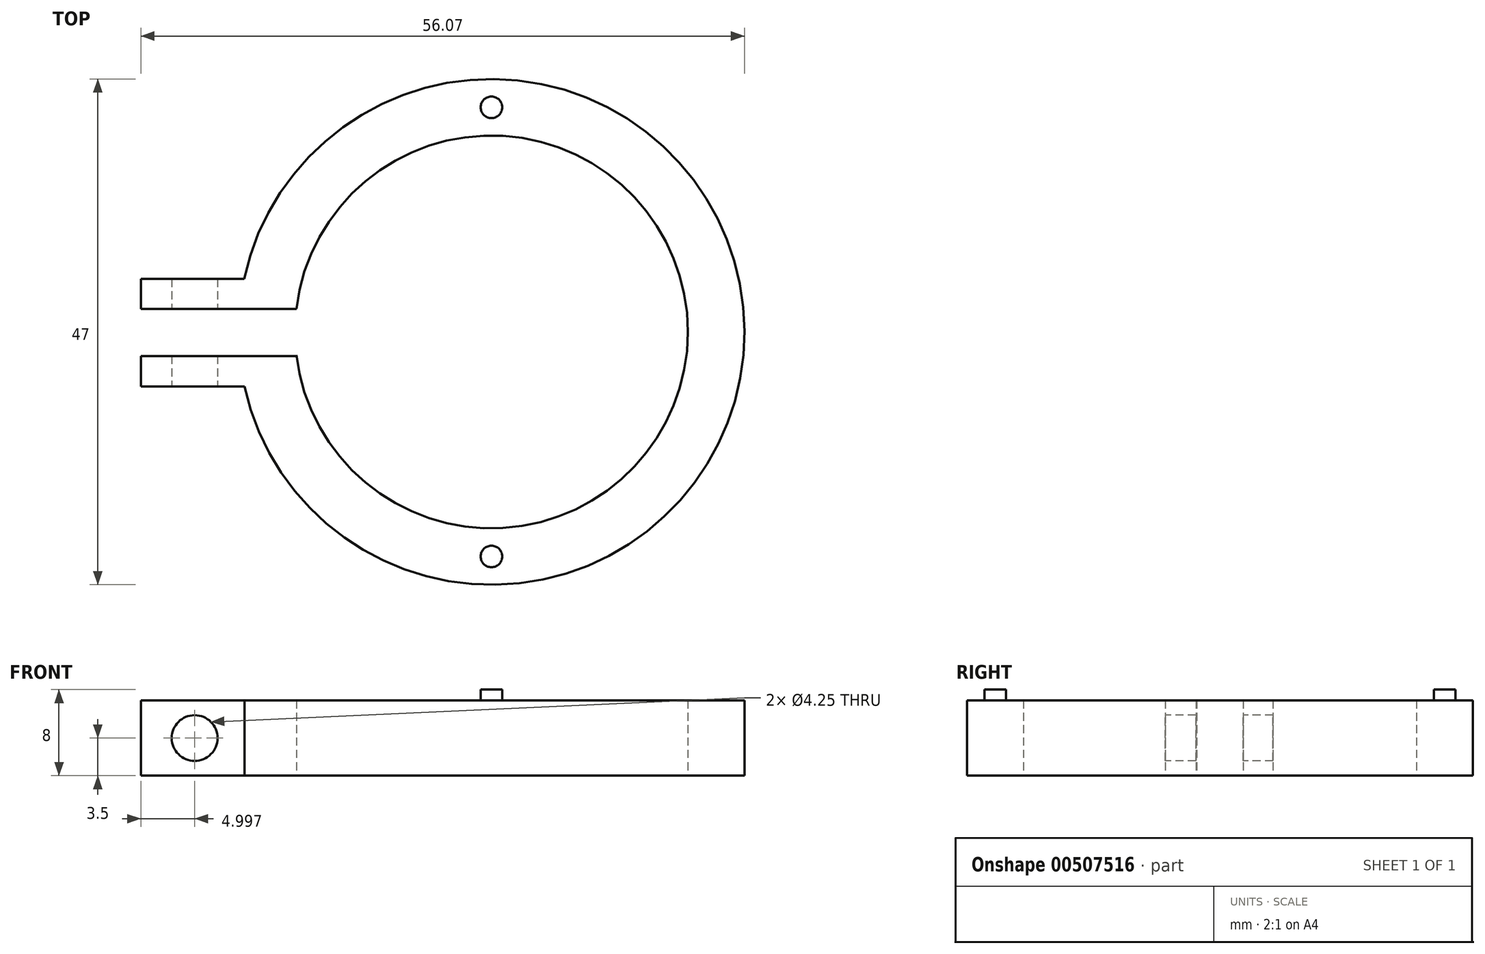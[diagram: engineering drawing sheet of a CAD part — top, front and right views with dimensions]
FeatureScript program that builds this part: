
annotation { "Feature Type Name" : "Feature", "Feature Type Description" : "" }
export const myFeature = defineFeature(function(context is Context, id is Id, definition is map)
    precondition{}
    {
        {
            var Q0;
            Q0=qCreatedBy(makeId("Top.planeOp"),FACE);
            var sketch = newSketch(context, id + "F0", { "sketchPlane" : qUnion([Q0])});
            skCircle(sketch, "E0", {"center": v(0, 0) * mm, "radius": 23.5 * mm});
            skCircle(sketch, "E1", {"center": v(0, 0) * mm, "radius": 18.25 * mm});
            skLineSegment(sketch, "E2.bottom", {"start": v(-17.57, 4.92) * mm, "end": v(-32.57, 4.92) * mm});
            skLineSegment(sketch, "E2.top", {"start": v(-17.57, -5.08) * mm, "end": v(-32.57, -5.08) * mm});
            skLineSegment(sketch, "E2.left", {"start": v(-17.57, 4.92) * mm, "end": v(-17.57, -5.08) * mm});
            skLineSegment(sketch, "E2.right", {"start": v(-32.57, 4.92) * mm, "end": v(-32.57, -5.08) * mm});
            skLineSegment(sketch, "E3.bottom", {"start": v(-18.12, 2.15) * mm, "end": v(-32.57, 2.15) * mm});
            skLineSegment(sketch, "E3.top", {"start": v(-18.12, -2.24) * mm, "end": v(-32.57, -2.24) * mm});
            skLineSegment(sketch, "E3.left", {"start": v(-18.12, 2.15) * mm, "end": v(-18.12, -2.24) * mm});
            skLineSegment(sketch, "E3.right", {"start": v(-32.57, 2.15) * mm, "end": v(-32.57, -2.24) * mm});
            skSolve(sketch);
        }
        {
            var Q0;
            {var subQ0=sQuery(id+"F0.wireOp",EDGE,"E2.bottom");var subQ1=sQuery(id+"F0.wireOp",EDGE,"E0");var subQ2=makeQuery(id+"F0.imprint","INTERSECT",VERTEX,{"derivedFrom":[subQ1,subQ0]});Q0=makeQuery(id+"F0.imprint","IMPRINT",FACE,{"disambiguationData":[TD([[makeQuery(id+"F0.imprint","IMPRINT",EDGE,{"disambiguationData":[TD([[subQ2,-1.0]])],"derivedFrom":subQ1}),-1.0]])]});}
            var Q1;
            {var subQ0=sQuery(id+"F0.wireOp",EDGE,"E2.top");var subQ1=sQuery(id+"F0.wireOp",EDGE,"E0");var subQ2=makeQuery(id+"F0.imprint","INTERSECT",VERTEX,{"derivedFrom":[subQ1,subQ0]});Q1=makeQuery(id+"F0.imprint","IMPRINT",FACE,{"disambiguationData":[TD([[makeQuery(id+"F0.imprint","IMPRINT",EDGE,{"disambiguationData":[TD([[subQ2,1.0]])],"derivedFrom":subQ1}),-1.0]])]});}
            var Q2;
            {var subQ3=sQuery(id+"F0.wireOp",EDGE,"E0");var subQ5=sQuery(id+"F0.wireOp",EDGE,"E2.bottom");var subQ9=makeQuery(id+"F0.imprint","INTERSECT",VERTEX,{"derivedFrom":[subQ3,subQ5]});Q2=makeQuery(id+"F0.imprint","IMPRINT",FACE,{"disambiguationData":[TD([[makeQuery(id+"F0.imprint","IMPRINT",EDGE,{"disambiguationData":[TD([[subQ9,1.0]])],"derivedFrom":subQ3}),1.0]])]});}
            var Q3;
            {var subQ0=sQuery(id+"F0.wireOp",EDGE,"E2.bottom");var subQ1=sQuery(id+"F0.wireOp",EDGE,"E0");var subQ2=makeQuery(id+"F0.imprint","INTERSECT",VERTEX,{"derivedFrom":[subQ1,subQ0]});Q3=makeQuery(id+"F0.imprint","IMPRINT",FACE,{"disambiguationData":[TD([[makeQuery(id+"F0.imprint","IMPRINT",EDGE,{"disambiguationData":[TD([[subQ2,-1.0]])],"derivedFrom":subQ1}),1.0]])]});}
            var Q4;
            {var subQ1=sQuery(id+"F0.wireOp",EDGE,"E2.top");var subQ5=sQuery(id+"F0.wireOp",EDGE,"E0");var subQ6=makeQuery(id+"F0.imprint","INTERSECT",VERTEX,{"derivedFrom":[subQ5,subQ1]});Q4=makeQuery(id+"F0.imprint","IMPRINT",FACE,{"disambiguationData":[TD([[makeQuery(id+"F0.imprint","IMPRINT",EDGE,{"disambiguationData":[TD([[subQ6,1.0]])],"derivedFrom":subQ5}),1.0]])]});}
            var Q5;
            Q5=qSketchRegion(id+"F2",true);
            extrude(context, id + "F1", {"entities" : qUnion([Q0, Q1, Q2, Q3, Q4, Q5]), "depth" : 7 * mm});
        }
        {
            var Q0;
            Q0=makeQuery(id+"F1.opExtrude","SWEPT_FACE",FACE,{"disambiguationData":[OSD([sQuery(id+"F0.wireOp",EDGE,"E2.top")])]});
            var sketch = newSketch(context, id + "F2", { "sketchPlane" : qUnion([Q0])});
            skCircle(sketch, "E4", {"center": v(-27.57, 3.5) * mm, "radius": 2.12 * mm});
            skSolve(sketch);
        }
        {
            var Q0;
            Q0=makeQuery(id+"F2.imprint","IMPRINT",FACE,{"disambiguationData":[TD([[makeQuery(id+"F2.imprint","IMPRINT",EDGE,{"derivedFrom":sQuery(id+"F2.wireOp",EDGE,"E4")}),1.0]])]});
            extrude(context, id + "F3", {"entities" : qUnion([Q0]), "operationType" : NewBodyOperationType.REMOVE, "oppositeDirection" : true, "depth" : 10 * mm});
        }
        {
            var Q0;
            Q0=makeQuery(id+"F1.opExtrude","CAP_FACE",FACE,{"disambiguationData":[OSD([sQuery(id+"F0.wireOp",EDGE,"E0"),sQuery(id+"F0.wireOp",EDGE,"E1"),sQuery(id+"F0.wireOp",EDGE,"E2.bottom"),sQuery(id+"F0.wireOp",EDGE,"E2.top"),sQuery(id+"F0.wireOp",EDGE,"E2.right"),sQuery(id+"F0.wireOp",EDGE,"E3.bottom"),sQuery(id+"F0.wireOp",EDGE,"E3.top"),sQuery(id+"F0.wireOp",EDGE,"E3.left")])],"isStart":false});
            var sketch = newSketch(context, id + "F4", { "sketchPlane" : qUnion([Q0])});
            skCircle(sketch, "E5", {"center": v(0, 20.88) * mm, "radius": 1 * mm});
            skCircle(sketch, "E6.1.0.0", {"center": v(0, -20.88) * mm, "radius": 1 * mm});
            skCircle(sketch, "E6.2.0.0", {"center": v(0, -62.62) * mm, "radius": 1 * mm});
            skLineSegment(sketch, "E6.direction1", {"start": v(0, 20.88) * mm, "end": v(0, -20.88) * mm, "construction": true});
            skSolve(sketch);
        }
        {
            var Q0;
            Q0=makeQuery(id+"F4.imprint","IMPRINT",FACE,{"disambiguationData":[TD([[makeQuery(id+"F4.imprint","IMPRINT",EDGE,{"derivedFrom":sQuery(id+"F4.wireOp",EDGE,"E6.1.0.0")}),1.0]])]});
            var Q1;
            Q1=makeQuery(id+"F4.imprint","IMPRINT",FACE,{"disambiguationData":[TD([[makeQuery(id+"F4.imprint","IMPRINT",EDGE,{"derivedFrom":sQuery(id+"F4.wireOp",EDGE,"E5")}),1.0]])]});
            var Q2;
            Q2=sQuery(id+"F4.wireOp",EDGE,"E5");
            extrude(context, id + "F5", {"entities" : qUnion([Q0, Q1]), "operationType" : NewBodyOperationType.ADD, "surfaceEntities" : qUnion([Q2]), "endBound" : BoundingType.SYMMETRIC, "depth" : 2 * mm});
        }
    });
